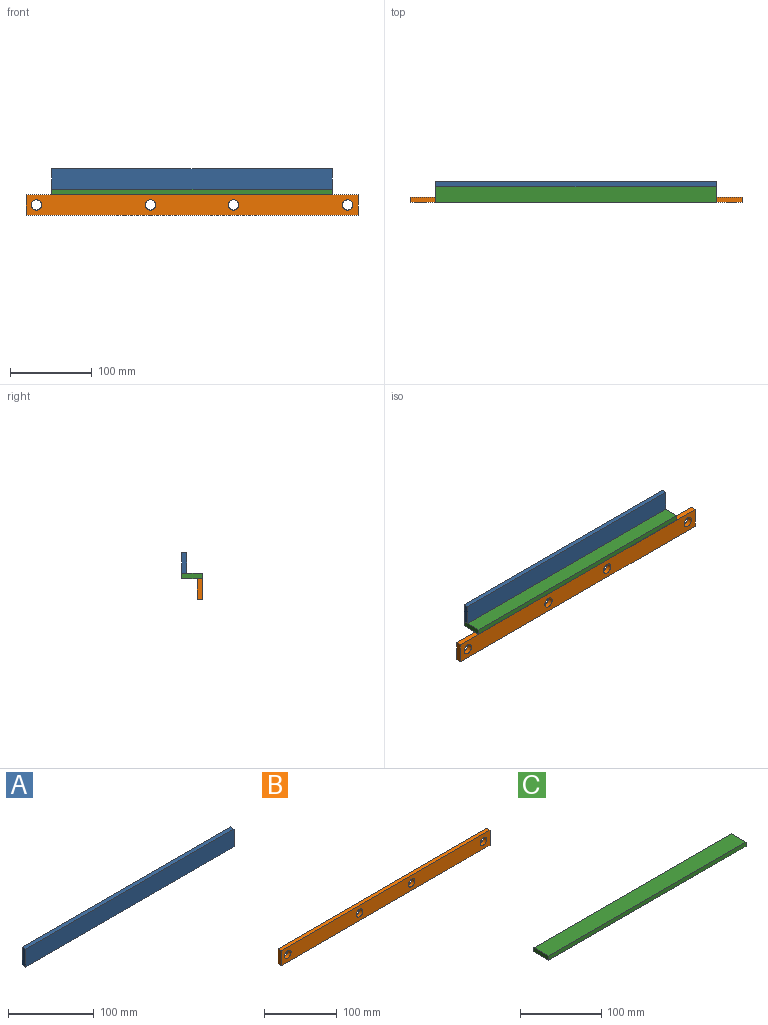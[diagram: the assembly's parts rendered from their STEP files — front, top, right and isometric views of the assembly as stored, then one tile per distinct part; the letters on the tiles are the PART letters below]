
ASSEMBLY  parts=3 mates=2
PART A: 6 faces, bbox 342.9x6.4x25.4 mm
  f0: plane 25.4x6.35mm, normal (-1,0,0), area 161.3mm2, adj f1,f3,f4,f5
  f1: plane 342.9x6.35mm, normal (0,0,-1), area 2177.4mm2, adj f0,f2,f4,f5
  f2: plane 25.4x6.35mm, normal (1,0,0), area 161.3mm2, adj f1,f3,f4,f5
  f3: plane 342.9x6.35mm, normal (0,0,1), area 2177.4mm2, adj f0,f2,f4,f5
  f4: plane 342.9x25.4mm, normal (0,-1,0), area 8709.7mm2, adj f0,f1,f2,f3
  f5: plane 342.9x25.4mm, normal (0,1,0), area 8709.7mm2, adj f0,f1,f2,f3
PART B: 10 faces, bbox 406.4x6.4x25.4 mm
  f0: plane 25.4x6.35mm, normal (-1,0,0), area 161.3mm2, adj f1,f3,f4,f5
  f1: plane 406.4x6.35mm, normal (0,0,-1), area 2580.6mm2, adj f0,f2,f4,f5
  f2: plane 25.4x6.35mm, normal (1,0,0), area 161.3mm2, adj f1,f3,f4,f5
  f3: plane 406.4x6.35mm, normal (0,0,1), area 2580.6mm2, adj f0,f2,f4,f5
  f4: plane 406.4x25.4mm, normal (0,-1,0), area 9815.9mm2, adj f0,f1,f2,f3,f6,f7,f8,f9
  f5: plane 406.4x25.4mm, normal (0,1,0), area 9815.9mm2, adj f0,f1,f2,f3,f6,f7,f8,f9
  f6: cylinder r=6.35mm len=12.7mm, axis (0,-1,0), area 253.4mm2, adj f4,f5
  f7: cylinder r=6.35mm len=12.7mm, axis (0,-1,0), area 253.4mm2, adj f4,f5
  f8: cylinder r=6.35mm len=12.7mm, axis (0,-1,0), area 253.4mm2, adj f4,f5
  f9: cylinder r=6.35mm len=12.7mm, axis (0,-1,0), area 253.4mm2, adj f4,f5
PART C: 6 faces, bbox 342.9x25.4x6.4 mm
  f0: plane 342.9x6.35mm, normal (0,1,0), area 2177.4mm2, adj f1,f3,f4,f5
  f1: plane 25.4x6.35mm, normal (-1,0,0), area 161.3mm2, adj f0,f2,f4,f5
  f2: plane 342.9x6.35mm, normal (0,-1,0), area 2177.4mm2, adj f1,f3,f4,f5
  f3: plane 25.4x6.35mm, normal (1,0,0), area 161.3mm2, adj f0,f2,f4,f5
  f4: plane 342.9x25.4mm, normal (0,0,1), area 8709.7mm2, adj f0,f1,f2,f3
  f5: plane 342.9x25.4mm, normal (0,0,-1), area 8709.7mm2, adj f0,f1,f2,f3
PLACE A t=(-6.35,0,0)mm
PLACE B t=(162.5,-19.05,106.58)mm
PLACE C t=(-42.38,29.79,-22.16)mm
MATE fastened C.f4 <-> A.f1  axis (0,0,1) through (-29.53,0,-15.81)mm
MATE fastened C.f5 <-> B.f3  axis (0,0,-1) through (-29.53,-25.4,-22.16)mm
